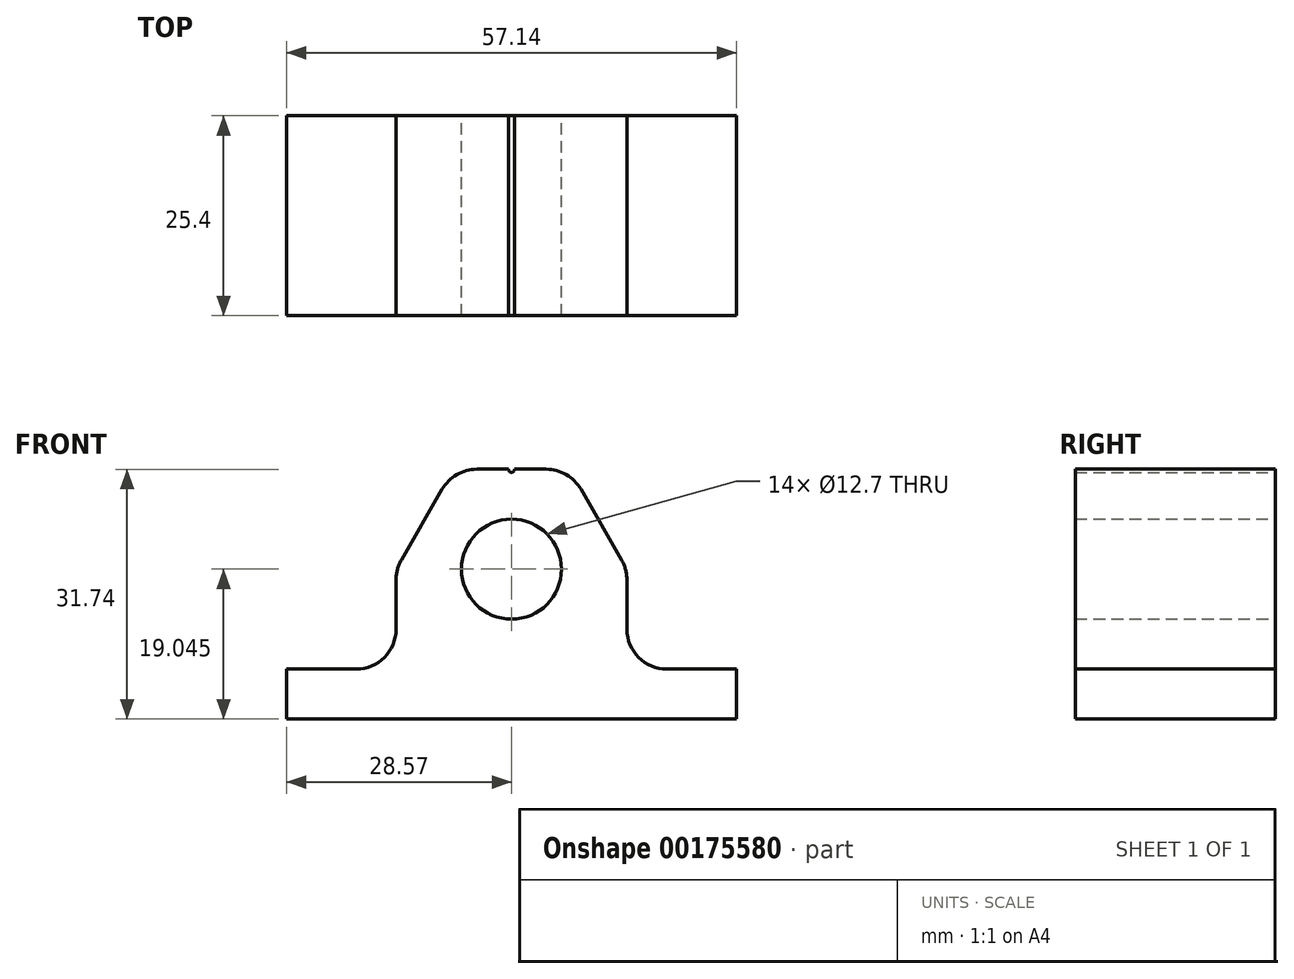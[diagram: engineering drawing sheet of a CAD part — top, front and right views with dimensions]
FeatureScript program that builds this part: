
annotation { "Feature Type Name" : "Feature", "Feature Type Description" : "" }
export const myFeature = defineFeature(function(context is Context, id is Id, definition is map)
    precondition{}
    {
        {
            var Q0;
            Q0=qCreatedBy(makeId("Front.planeOp"),FACE);
            var sketch = newSketch(context, id + "F0", { "sketchPlane" : qUnion([Q0])});
            skLineSegment(sketch, "E0.bottom", {"start": v(-28.58, 3.18) * mm, "end": v(28.58, 3.18) * mm});
            skLineSegment(sketch, "E0.top", {"start": v(-28.57, -3.17) * mm, "end": v(28.57, -3.17) * mm});
            skLineSegment(sketch, "E0.left", {"start": v(-28.58, 3.18) * mm, "end": v(-28.58, -3.18) * mm});
            skLineSegment(sketch, "E0.right", {"start": v(28.58, 3.18) * mm, "end": v(28.58, -3.18) * mm});
            skPoint(sketch, "E0.middle", {"position": v(0, 0) * mm});
            skLineSegment(sketch, "E1", {"start": v(0, 3.18) * mm, "end": v(0, 15.88) * mm});
            skPoint(sketch, "E1.endSnap0", {"position": v(0, 3.18) * mm});
            skCircle(sketch, "E2.cCircle", {"center": v(0, 15.88) * mm, "radius": 12.7 * mm, "construction": true});
            skLineSegment(sketch, "E2.0", {"start": v(7.33, 3.18) * mm, "end": v(-7.33, 3.18) * mm});
            skLineSegment(sketch, "E2.1", {"start": v(-7.33, 3.18) * mm, "end": v(-14.66, 15.88) * mm});
            skLineSegment(sketch, "E2.2", {"start": v(-14.66, 15.88) * mm, "end": v(-7.33, 28.58) * mm});
            skLineSegment(sketch, "E2.3", {"start": v(-7.33, 28.58) * mm, "end": v(7.33, 28.58) * mm});
            skLineSegment(sketch, "E2.4", {"start": v(7.33, 28.58) * mm, "end": v(14.66, 15.88) * mm});
            skLineSegment(sketch, "E2.5", {"start": v(14.66, 15.88) * mm, "end": v(7.33, 3.17) * mm});
            skLineSegment(sketch, "E3", {"start": v(-14.66, 15.88) * mm, "end": v(-14.66, 3.18) * mm});
            skLineSegment(sketch, "E4", {"start": v(14.66, 15.88) * mm, "end": v(14.66, 3.18) * mm});
            skCircle(sketch, "E5", {"center": v(0, 15.88) * mm, "radius": 6.35 * mm});
            skPoint(sketch, "E6", {"position": v(0, 28.58) * mm});
            skPoint(sketch, "E7", {"position": v(-0.4, 28.58) * mm});
            skPoint(sketch, "E8", {"position": v(0.4, 28.58) * mm});
            skArc(sketch, "E9", {"start": v(-0.4, 28.58) * mm, "mid": v(0, 28.18) * mm, "end": v(0.4, 28.58) * mm});
            skSolve(sketch);
        }
        {
            var Q0;
            {var subQ0=sQuery(id+"F0.wireOp",EDGE,"E2.1");Q0=makeQuery(id+"F0.imprint","IMPRINT",FACE,{"disambiguationData":[TD([[makeQuery(id+"F0.imprint","IMPRINT",EDGE,{"derivedFrom":subQ0}),1.0]])]});}
            var Q1;
            {var subQ0=sQuery(id+"F0.wireOp",EDGE,"E2.5");Q1=makeQuery(id+"F0.imprint","IMPRINT",FACE,{"disambiguationData":[TD([[makeQuery(id+"F0.imprint","IMPRINT",EDGE,{"derivedFrom":subQ0}),1.0]])]});}
            var Q2;
            Q2=makeQuery(id+"F0.imprint","IMPRINT",FACE,{"disambiguationData":[TD([[makeQuery(id+"F0.imprint","IMPRINT",EDGE,{"derivedFrom":sQuery(id+"F0.wireOp",EDGE,"E0.top")}),1.0]])]});
            var Q3;
            {var subQ1=sQuery(id+"F0.wireOp",EDGE,"E2.1");Q3=makeQuery(id+"F0.imprint","IMPRINT",FACE,{"disambiguationData":[TD([[makeQuery(id+"F0.imprint","IMPRINT",EDGE,{"derivedFrom":subQ1}),-1.0]])]});}
            extrude(context, id + "F1", {"entities" : qUnion([Q0, Q1, Q2, Q3]), "depth" : 25.4 * mm});
        }
        {
            var Q0;
            Q0=makeQuery(id+"F1.opExtrude","SWEPT_EDGE",EDGE,{"disambiguationData":[OSD([sQuery(id+"F0.wireOp",EDGE,"E2.2"),sQuery(id+"F0.wireOp",EDGE,"E2.3")])]});
            var Q1;
            Q1=makeQuery(id+"F1.opExtrude","SWEPT_EDGE",EDGE,{"disambiguationData":[OSD([sQuery(id+"F0.wireOp",EDGE,"E2.3"),sQuery(id+"F0.wireOp",EDGE,"E2.4")])]});
            var Q2;
            Q2=makeQuery(id+"F1.opExtrude","SWEPT_EDGE",EDGE,{"disambiguationData":[OSD([sQuery(id+"F0.wireOp",EDGE,"E2.4"),sQuery(id+"F0.wireOp",EDGE,"E2.5"),sQuery(id+"F0.wireOp",EDGE,"E4")])]});
            var Q3;
            Q3=makeQuery(id+"F1.opExtrude","SWEPT_EDGE",EDGE,{"disambiguationData":[OSD([sQuery(id+"F0.wireOp",EDGE,"E0.bottom"),sQuery(id+"F0.wireOp",EDGE,"E4")])]});
            var Q4;
            Q4=makeQuery(id+"F1.opExtrude","SWEPT_EDGE",EDGE,{"disambiguationData":[OSD([sQuery(id+"F0.wireOp",EDGE,"E2.1"),sQuery(id+"F0.wireOp",EDGE,"E2.2"),sQuery(id+"F0.wireOp",EDGE,"E3")])]});
            var Q5;
            Q5=makeQuery(id+"F1.opExtrude","SWEPT_EDGE",EDGE,{"disambiguationData":[OSD([sQuery(id+"F0.wireOp",EDGE,"E0.bottom"),sQuery(id+"F0.wireOp",EDGE,"E3")])]});
            fillet(context, id + "F2", {"entities" : qUnion([Q0, Q1, Q2, Q3, Q4, Q5]), "radius" : 5.08 * mm, "tangentPropagation" : true, "allowEdgeOverflow" : false});
        }
    });
